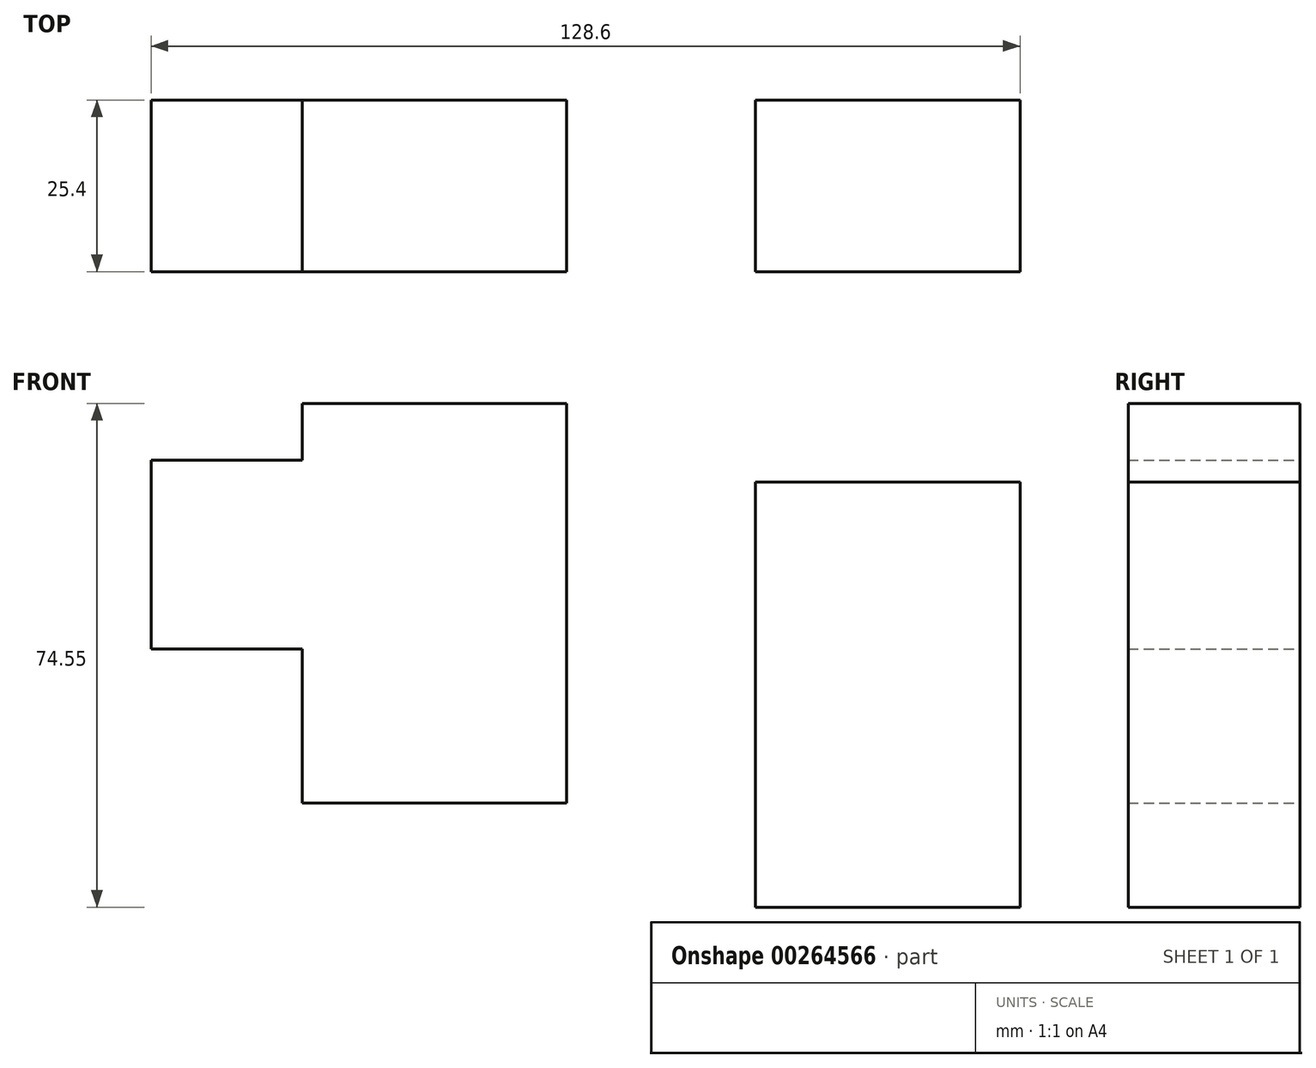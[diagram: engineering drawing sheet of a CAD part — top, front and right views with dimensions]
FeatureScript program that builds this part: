
annotation { "Feature Type Name" : "Feature", "Feature Type Description" : "" }
export const myFeature = defineFeature(function(context is Context, id is Id, definition is map)
    precondition{}
    {
        {
            var Q0;
            Q0=qCreatedBy(makeId("Front.planeOp"),FACE);
            var sketch = newSketch(context, id + "F0", { "sketchPlane" : qUnion([Q0])});
            skLineSegment(sketch, "E0.bottom", {"start": v(-43.8, 0) * mm, "end": v(-4.66, 0) * mm});
            skLineSegment(sketch, "E0.top", {"start": v(-43.8, -59.17) * mm, "end": v(-4.66, -59.17) * mm});
            skLineSegment(sketch, "E0.left", {"start": v(-43.8, 0) * mm, "end": v(-43.8, -59.17) * mm});
            skLineSegment(sketch, "E0.right", {"start": v(-4.66, 0) * mm, "end": v(-4.66, -59.17) * mm});
            skLineSegment(sketch, "E1.bottom", {"start": v(23.3, -11.65) * mm, "end": v(62.44, -11.65) * mm});
            skLineSegment(sketch, "E1.top", {"start": v(23.3, -74.55) * mm, "end": v(62.44, -74.55) * mm});
            skLineSegment(sketch, "E1.left", {"start": v(23.3, -11.65) * mm, "end": v(23.3, -74.55) * mm});
            skLineSegment(sketch, "E1.right", {"start": v(62.44, -11.65) * mm, "end": v(62.44, -74.55) * mm});
            skLineSegment(sketch, "E2.bottom", {"start": v(77.81, -36.34) * mm, "end": v(-66.16, -36.34) * mm});
            skLineSegment(sketch, "E2.top", {"start": v(77.81, -8.39) * mm, "end": v(-66.16, -8.39) * mm});
            skLineSegment(sketch, "E2.left", {"start": v(77.81, -36.34) * mm, "end": v(77.81, -8.39) * mm});
            skLineSegment(sketch, "E2.right", {"start": v(-66.16, -36.34) * mm, "end": v(-66.16, -8.39) * mm});
            skSolve(sketch);
        }
        {
            var Q0;
            {var subQ0=sQuery(id+"F0.wireOp",EDGE,"E2.top");var subQ1=sQuery(id+"F0.wireOp",EDGE,"E0.left");var subQ2=makeQuery(id+"F0.imprint","INTERSECT",VERTEX,{"derivedFrom":[subQ1,subQ0]});Q0=makeQuery(id+"F0.imprint","IMPRINT",FACE,{"disambiguationData":[TD([[makeQuery(id+"F0.imprint","IMPRINT",EDGE,{"disambiguationData":[TD([[subQ2,-1.0]])],"derivedFrom":subQ1}),1.0]])]});}
            var Q1;
            {var subQ0=sQuery(id+"F0.wireOp",EDGE,"E1.bottom");Q1=makeQuery(id+"F0.imprint","IMPRINT",FACE,{"disambiguationData":[TD([[makeQuery(id+"F0.imprint","IMPRINT",EDGE,{"derivedFrom":subQ0}),-1.0]])]});}
            var Q2;
            {var subQ0=sQuery(id+"F0.wireOp",EDGE,"E1.top");Q2=makeQuery(id+"F0.imprint","IMPRINT",FACE,{"disambiguationData":[TD([[makeQuery(id+"F0.imprint","IMPRINT",EDGE,{"derivedFrom":subQ0}),1.0]])]});}
            var Q3;
            {var subQ0=sQuery(id+"F0.wireOp",EDGE,"E0.top");Q3=makeQuery(id+"F0.imprint","IMPRINT",FACE,{"disambiguationData":[TD([[makeQuery(id+"F0.imprint","IMPRINT",EDGE,{"derivedFrom":subQ0}),1.0]])]});}
            var Q4;
            {var subQ5=sQuery(id+"F0.wireOp",EDGE,"E2.right");Q4=makeQuery(id+"F0.imprint","IMPRINT",FACE,{"disambiguationData":[TD([[makeQuery(id+"F0.imprint","IMPRINT",EDGE,{"derivedFrom":subQ5}),-1.0]])]});}
            var Q5;
            {var subQ0=sQuery(id+"F0.wireOp",EDGE,"E0.bottom");Q5=makeQuery(id+"F0.imprint","IMPRINT",FACE,{"disambiguationData":[TD([[makeQuery(id+"F0.imprint","IMPRINT",EDGE,{"derivedFrom":subQ0}),-1.0]])]});}
            extrude(context, id + "F1", {"entities" : qUnion([Q0, Q1, Q2, Q3, Q4, Q5]), "depth" : 25.4 * mm});
        }
    });
